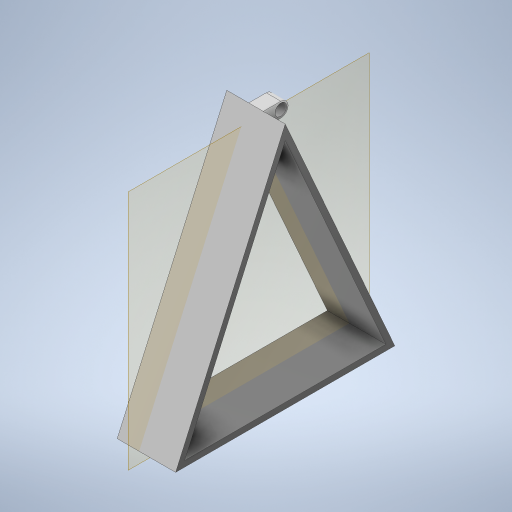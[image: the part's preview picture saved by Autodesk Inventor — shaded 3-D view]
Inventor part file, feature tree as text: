
AUTODESK INVENTOR PART (.ipt)
format: ipt  version: 2023 (Build 270158000, 158)  size: 282,112 bytes
history: native  units: mm
features: extrude x3, sketch x3, shell x1, plane x1, fillet x1
ambient origin geometry x8: Origin, YZ Plane, XZ Plane, XY Plane, X Axis, Y Axis, Z Axis, Center Point
bodies: Volumenkörper1 (feature_tree)
feature tree (9):
  extrude  "Extrusion1"  TaperAngle=90.0deg  [1 undecoded]
  shell  "Wandung1"  Thickness=75.0mm
  plane  "Arbeitsebene3"
  extrude  "Extrusion6"  Depth=40.0mm TaperAngle=0.0deg
  fillet  "Rundung1"  Radius=4.0mm
  extrude  "Extrusion7"  Depth=5.0mm
  sketch  "Skizze1"  dims[d0=150.0mm d1=90.0deg d2=75.0mm]
  sketch  "Skizze7"  dims[d3=169.007mm d4=40.0mm d5=0.0mm d6=4.0mm]
  sketch  "Skizze8"  dims[d23=15.0mm d24=17.0mm d25=10.0mm d26=10.0mm d27=0.0mm d28=5.0mm d29=8.0mm d30=0.0mm d31=0.0mm d20=1.0mm d21=1.0mm d22=1.0mm d32=0.15mm d33=0.25mm d34=0.375mm d35=14.3117mm d36=0.75mm d37=20.594885mm d38=0.0625mm d39=0.75mm d40=0.375mm]
note: 1 required parameter value undecoded (feature->parameter linkage not recoverable at this tier; creation-order binding heuristic only, values carry confidence <= 0.55)
